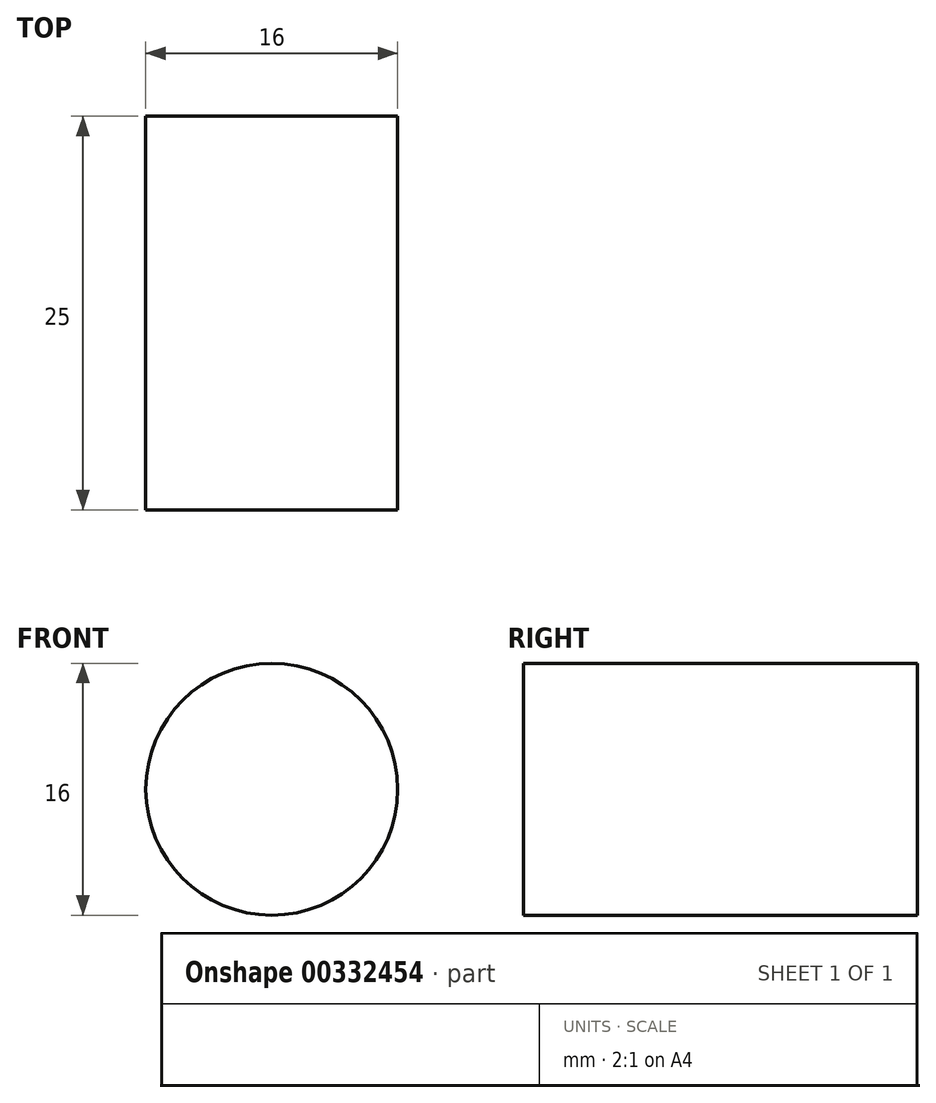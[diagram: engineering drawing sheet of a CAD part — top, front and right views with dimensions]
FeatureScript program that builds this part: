
annotation { "Feature Type Name" : "Feature", "Feature Type Description" : "" }
export const myFeature = defineFeature(function(context is Context, id is Id, definition is map)
    precondition{}
    {
        {
            var Q0;
            Q0=qCreatedBy(makeId("Front.planeOp"),FACE);
            var sketch = newSketch(context, id + "F0", { "sketchPlane" : qUnion([Q0])});
            skCircle(sketch, "E0", {"center": v(0, 0) * mm, "radius": 8 * mm});
            skSolve(sketch);
        }
        {
            var Q0;
            Q0 = qSketchRegion(id + "F0", true);
            extrude(context, id + "F1", {"entities" : qUnion([Q0]), "endBound" : BoundingType.SYMMETRIC, "depth" : 25 * mm});
        }
    });
